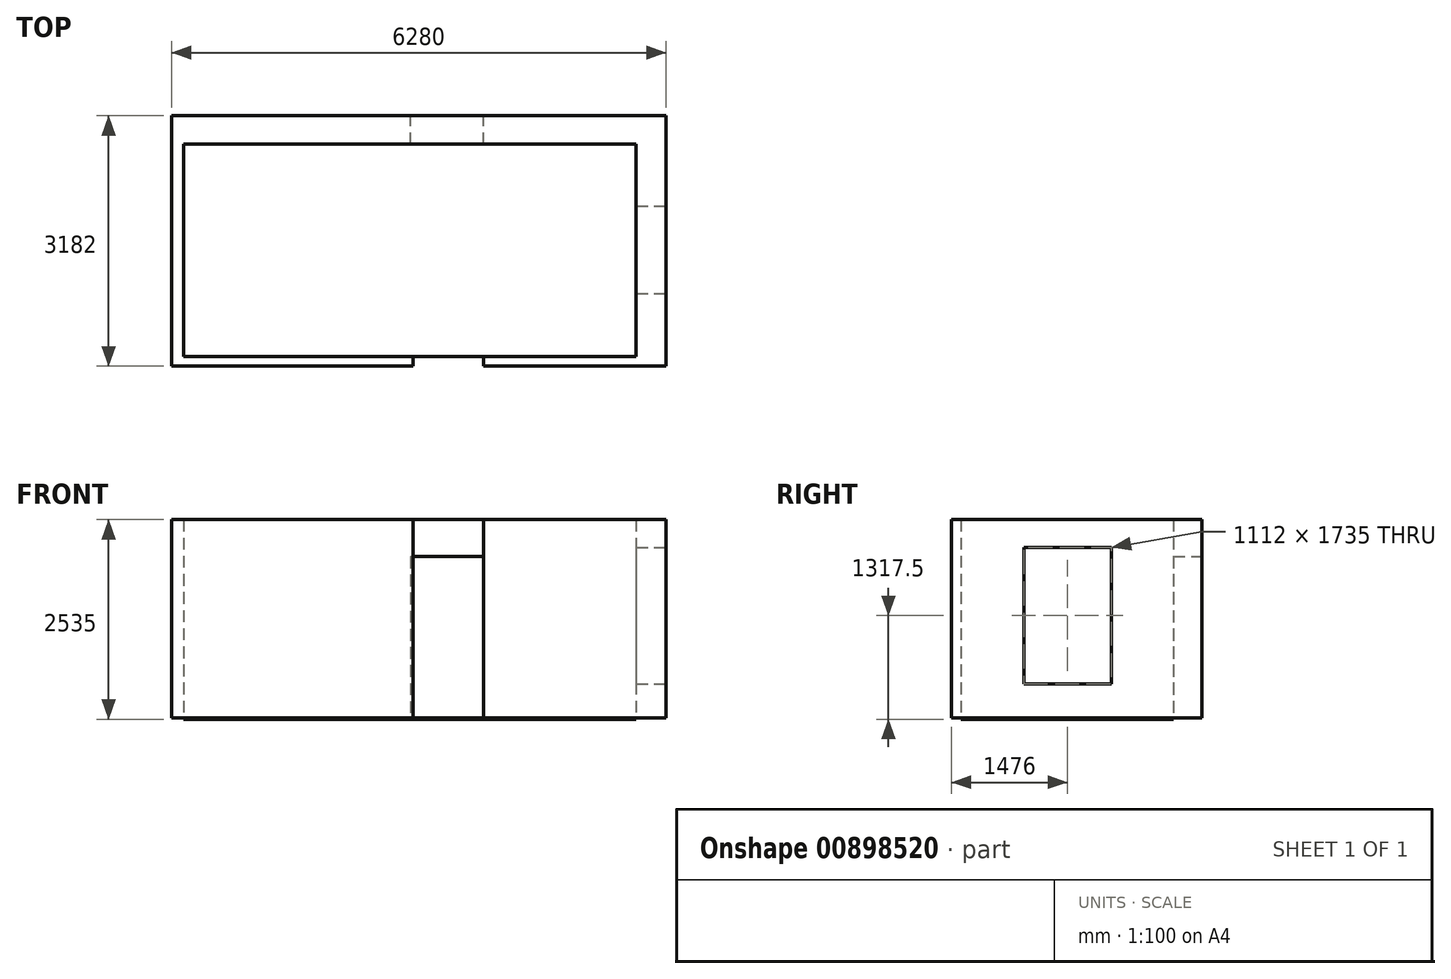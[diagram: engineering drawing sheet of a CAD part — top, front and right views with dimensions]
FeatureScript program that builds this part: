
annotation { "Feature Type Name" : "Feature", "Feature Type Description" : "" }
export const myFeature = defineFeature(function(context is Context, id is Id, definition is map)
    precondition{}
    {
        {
            var Q0;
            Q0=qCreatedBy(makeId("Top.planeOp"),FACE);
            var sketch = newSketch(context, id + "F0", { "sketchPlane" : qUnion([Q0])});
            skLineSegment(sketch, "E0.bottom", {"start": v(2875, -1350) * mm, "end": v(-2875, -1350) * mm});
            skLineSegment(sketch, "E0.top", {"start": v(2875, 1350) * mm, "end": v(-2875, 1350) * mm});
            skLineSegment(sketch, "E0.left", {"start": v(2875, -1350) * mm, "end": v(2875, 1350) * mm});
            skLineSegment(sketch, "E0.right", {"start": v(-2875, -1350) * mm, "end": v(-2875, 1350) * mm});
            skPoint(sketch, "E0.middle", {"position": v(0, 0) * mm});
            skLineSegment(sketch, "E1.bottom", {"start": v(7, 1350) * mm, "end": v(937, 1350) * mm});
            skLineSegment(sketch, "E1.top", {"start": v(7, 1712) * mm, "end": v(937, 1712) * mm});
            skLineSegment(sketch, "E1.left", {"start": v(7, 1350) * mm, "end": v(7, 1712) * mm});
            skLineSegment(sketch, "E1.right", {"start": v(937, 1350) * mm, "end": v(937, 1712) * mm});
            skLineSegment(sketch, "E2.bottom", {"start": v(40, -1350) * mm, "end": v(940, -1350) * mm});
            skLineSegment(sketch, "E2.top", {"start": v(40, -1470) * mm, "end": v(940, -1470) * mm});
            skLineSegment(sketch, "E2.left", {"start": v(40, -1350) * mm, "end": v(40, -1470) * mm});
            skLineSegment(sketch, "E2.right", {"start": v(940, -1350) * mm, "end": v(940, -1470) * mm});
            skLineSegment(sketch, "E3.bottom", {"start": v(2875, -550) * mm, "end": v(3255, -550) * mm});
            skLineSegment(sketch, "E3.top", {"start": v(2875, 562) * mm, "end": v(3255, 562) * mm});
            skLineSegment(sketch, "E3.left", {"start": v(2875, -550) * mm, "end": v(2875, 562) * mm});
            skLineSegment(sketch, "E3.right", {"start": v(3255, -550) * mm, "end": v(3255, 562) * mm});
            skLineSegment(sketch, "E4", {"start": v(940, -1470) * mm, "end": v(3255, -1470) * mm});
            skLineSegment(sketch, "E5", {"start": v(3255, -1470) * mm, "end": v(3255, 1712) * mm});
            skLineSegment(sketch, "E6", {"start": v(3255, 1712) * mm, "end": v(-3025, 1712) * mm});
            skPoint(sketch, "E6.endSnap0", {"position": v(472, 1712) * mm});
            skLineSegment(sketch, "E7", {"start": v(-3025, 1712) * mm, "end": v(-3025, -1470) * mm});
            skLineSegment(sketch, "E8", {"start": v(-3025, -1470) * mm, "end": v(40, -1470) * mm});
            skSolve(sketch);
        }
        {
            var Q0;
            {var subQ1=sQuery(id+"F0.wireOp",EDGE,"E0.right");Q0=makeQuery(id+"F0.imprint","IMPRINT",FACE,{"disambiguationData":[TD([[makeQuery(id+"F0.imprint","IMPRINT",EDGE,{"derivedFrom":subQ1}),1.0]])]});}
            var Q1;
            {var subQ0=sQuery(id+"F0.wireOp",EDGE,"E1.right");Q1=makeQuery(id+"F0.imprint","IMPRINT",FACE,{"disambiguationData":[TD([[makeQuery(id+"F0.imprint","IMPRINT",EDGE,{"derivedFrom":subQ0}),-1.0]])]});}
            var Q2;
            {var subQ0=sQuery(id+"F0.wireOp",EDGE,"E2.right");Q2=makeQuery(id+"F0.imprint","IMPRINT",FACE,{"disambiguationData":[TD([[makeQuery(id+"F0.imprint","IMPRINT",EDGE,{"derivedFrom":subQ0}),1.0]])]});}
            extrude(context, id + "F1", {"entities" : qUnion([Q0, Q1, Q2]), "depth" : 2520 * mm, "offsetDistance" : 25 * mm});
        }
        {
            var Q0;
            {var subQ0=sQuery(id+"F0.wireOp",EDGE,"E3.bottom");Q0=makeQuery(id+"F0.imprint","IMPRINT",FACE,{"disambiguationData":[TD([[makeQuery(id+"F0.imprint","IMPRINT",EDGE,{"derivedFrom":subQ0}),1.0]])]});}
            extrude(context, id + "F2", {"entities" : qUnion([Q0]), "operationType" : NewBodyOperationType.ADD, "depth" : 435 * mm, "offsetDistance" : 25 * mm});
        }
        {
            var Q0;
            Q0=makeQuery(id+"F1.opExtrude","CAP_FACE",FACE,{"disambiguationData":[OSD([sQuery(id+"F0.wireOp",EDGE,"E0.top"),sQuery(id+"F0.wireOp",EDGE,"E0.left"),sQuery(id+"F0.wireOp",EDGE,"E1.right"),sQuery(id+"F0.wireOp",EDGE,"E3.top"),sQuery(id+"F0.wireOp",EDGE,"E5"),sQuery(id+"F0.wireOp",EDGE,"E6")])],"isStart":false});
            var sketch = newSketch(context, id + "F3", { "sketchPlane" : qUnion([Q0])});
            skLineSegment(sketch, "E9.bottom", {"start": v(2875, 562) * mm, "end": v(3255, 562) * mm});
            skLineSegment(sketch, "E9.top", {"start": v(2875, -550) * mm, "end": v(3255, -550) * mm});
            skLineSegment(sketch, "E9.left", {"start": v(2875, 562) * mm, "end": v(2875, -550) * mm});
            skLineSegment(sketch, "E9.right", {"start": v(3255, 562) * mm, "end": v(3255, -550) * mm});
            skSolve(sketch);
        }
        {
            var Q0;
            Q0=makeQuery(id+"F3.imprint","IMPRINT",FACE,{"disambiguationData":[TD([[makeQuery(id+"F3.imprint","IMPRINT",EDGE,{"derivedFrom":sQuery(id+"F3.wireOp",EDGE,"E9.bottom")}),-1.0]])]});
            extrude(context, id + "F4", {"entities" : qUnion([Q0]), "operationType" : NewBodyOperationType.ADD, "oppositeDirection" : true, "depth" : 350 * mm, "offsetDistance" : 25 * mm});
        }
        {
            var Q0;
            Q0=makeQuery(id+"F1.opExtrude","CAP_FACE",FACE,{"disambiguationData":[OSD([sQuery(id+"F0.wireOp",EDGE,"E0.bottom"),sQuery(id+"F0.wireOp",EDGE,"E0.top"),sQuery(id+"F0.wireOp",EDGE,"E0.right"),sQuery(id+"F0.wireOp",EDGE,"E1.left"),sQuery(id+"F0.wireOp",EDGE,"E2.left"),sQuery(id+"F0.wireOp",EDGE,"E6"),sQuery(id+"F0.wireOp",EDGE,"E7"),sQuery(id+"F0.wireOp",EDGE,"E8")])],"isStart":false});
            var sketch = newSketch(context, id + "F5", { "sketchPlane" : qUnion([Q0])});
            skLineSegment(sketch, "E10.bottom", {"start": v(7, 1350) * mm, "end": v(937, 1350) * mm});
            skLineSegment(sketch, "E10.top", {"start": v(7, 1712) * mm, "end": v(937, 1712) * mm});
            skLineSegment(sketch, "E10.left", {"start": v(7, 1350) * mm, "end": v(7, 1712) * mm});
            skLineSegment(sketch, "E10.right", {"start": v(937, 1350) * mm, "end": v(937, 1712) * mm});
            skSolve(sketch);
        }
        {
            var Q0;
            Q0=makeQuery(id+"F5.imprint","IMPRINT",FACE,{"disambiguationData":[TD([[makeQuery(id+"F5.imprint","IMPRINT",EDGE,{"derivedFrom":sQuery(id+"F5.wireOp",EDGE,"E10.bottom")}),1.0]])]});
            extrude(context, id + "F6", {"entities" : qUnion([Q0]), "operationType" : NewBodyOperationType.ADD, "oppositeDirection" : true, "depth" : 468 * mm, "offsetDistance" : 25 * mm});
        }
        {
            var Q0;
            Q0=makeQuery(id+"F1.opExtrude","CAP_FACE",FACE,{"disambiguationData":[OSD([sQuery(id+"F0.wireOp",EDGE,"E0.bottom"),sQuery(id+"F0.wireOp",EDGE,"E0.top"),sQuery(id+"F0.wireOp",EDGE,"E0.right"),sQuery(id+"F0.wireOp",EDGE,"E1.left"),sQuery(id+"F0.wireOp",EDGE,"E2.left"),sQuery(id+"F0.wireOp",EDGE,"E6"),sQuery(id+"F0.wireOp",EDGE,"E7"),sQuery(id+"F0.wireOp",EDGE,"E8")])],"isStart":true});
            var sketch = newSketch(context, id + "F7", { "sketchPlane" : qUnion([Q0])});
            skLineSegment(sketch, "E11.bottom", {"start": v(-2875, 1350) * mm, "end": v(2875, 1350) * mm});
            skLineSegment(sketch, "E11.top", {"start": v(-2875, -1350) * mm, "end": v(2875, -1350) * mm});
            skLineSegment(sketch, "E11.left", {"start": v(-2875, 1350) * mm, "end": v(-2875, -1350) * mm});
            skLineSegment(sketch, "E11.right", {"start": v(2875, 1350) * mm, "end": v(2875, -1350) * mm});
            skSolve(sketch);
        }
        {
            var Q0;
            {var subQ0=sQuery(id+"F7.wireOp",EDGE,"E11.left");Q0=makeQuery(id+"F7.imprint","IMPRINT",FACE,{"disambiguationData":[TD([[makeQuery(id+"F7.imprint","IMPRINT",EDGE,{"derivedFrom":subQ0}),1.0]])]});}
            extrude(context, id + "F8", {"entities" : qUnion([Q0]), "depth" : 15 * mm, "offsetDistance" : 25 * mm});
        }
    });
